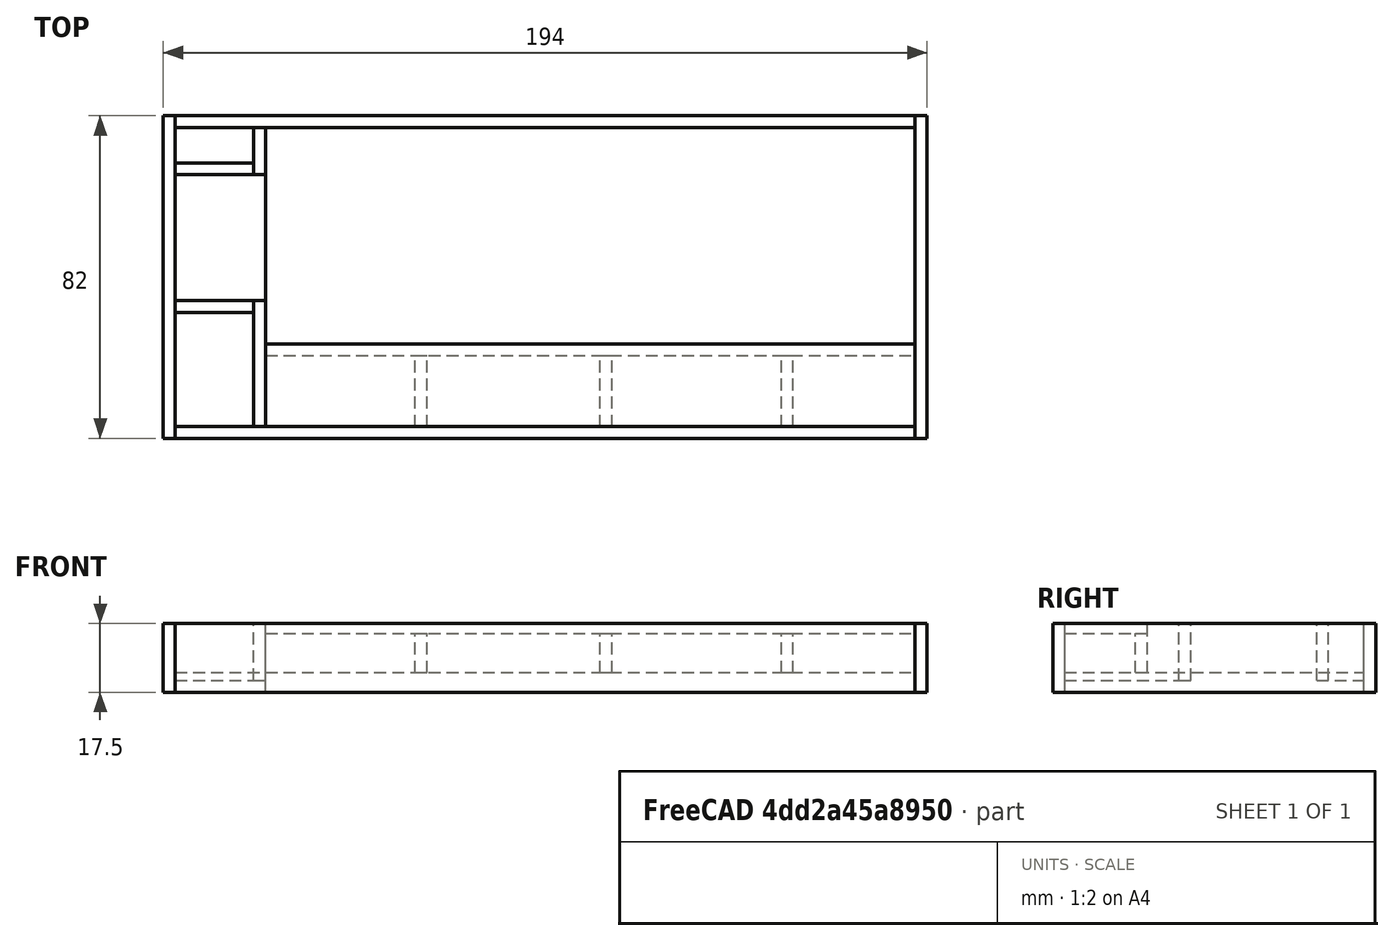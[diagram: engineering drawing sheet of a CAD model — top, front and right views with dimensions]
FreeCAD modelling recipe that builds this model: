
FCSTD DOCUMENT  (FreeCAD 0.15R4671 (Git))
Label: lcd breadboard case
License: All rights reserved
LicenseURL: http://en.wikipedia.org/wiki/All_rights_reserved
objects: Part::Box×15
note: 15 computed .brp shape members not serialized (recipe doc carries the construction recipe); baked Part::Feature solids carry a one-line shape summary decoded from their .brp

FEATURE [Part::Box] Box  label="base"
  Height = 5
  Length = 165
  Width = 76
FEATURE [Part::Box] Box001  label="platform support"
  Height = 10
  Length = 3
  Placement = pos=(85,0,5) rot=(0,0,1;0rad)
  Width = 18
FEATURE [Part::Box] Box002  label="platform"
  Height = 2.5
  Length = 165
  Placement = pos=(0,0,15) rot=(0,0,1;0rad)
  Width = 21
FEATURE [Part::Box] Box004  label="side 001"
  Height = 17.5
  Length = 188
  Placement = pos=(-23,-3,0) rot=(0,0,1;0rad)
  Width = 3
FEATURE [Part::Box] Box005  label="side 002"
  Height = 17.5
  Length = 188
  Placement = pos=(-23,76,0) rot=(0,0,1;0rad)
  Width = 3
FEATURE [Part::Box] Box006  label="side 003"
  Height = 14.5
  Length = 3
  Placement = pos=(-3,0,3) rot=(0,0,1;0rad)
  Width = 32
FEATURE [Part::Box] Box007  label="side 004"
  Height = 14.5
  Length = 3
  Placement = pos=(-3,64,3) rot=(0,0,1;0rad)
  Width = 12
FEATURE [Part::Box] Box008  label="side 005"
  Height = 17.5
  Length = 3
  Placement = pos=(165,-3,0) rot=(0,0,1;0rad)
  Width = 82
FEATURE [Part::Box] Box009  label="platform support001"
  Height = 10
  Length = 165
  Placement = pos=(0,18,5) rot=(0,0,1;0rad)
  Width = 3
FEATURE [Part::Box] Box010  label="platform support002"
  Height = 10
  Length = 3
  Placement = pos=(131,0,5) rot=(0,0,1;0rad)
  Width = 18
FEATURE [Part::Box] Box011  label="base 002"
  Height = 5
  Length = 23
  Placement = pos=(-23,0,0) rot=(0,0,1;0rad)
  Width = 76
FEATURE [Part::Box] Box012  label="side 006"
  Height = 14.5
  Length = 20
  Placement = pos=(-23,64,3) rot=(0,0,1;0rad)
  Width = 3
FEATURE [Part::Box] Box013  label="side 007"
  Height = 14.5
  Length = 20
  Placement = pos=(-23,29,3) rot=(0,0,1;0rad)
  Width = 3
FEATURE [Part::Box] Box014  label="side 008"
  Height = 17.5
  Length = 3
  Placement = pos=(-26,-3,0) rot=(0,0,1;0rad)
  Width = 82
FEATURE [Part::Box] Box015  label="platform support003"
  Height = 10
  Length = 3
  Placement = pos=(38,0,5) rot=(0,0,1;0rad)
  Width = 18
